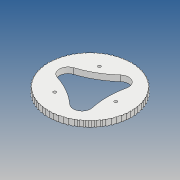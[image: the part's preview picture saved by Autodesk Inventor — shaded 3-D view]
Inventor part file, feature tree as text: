
AUTODESK INVENTOR PART (.ipt)
format: ipt  version: 2017 (Build 210142000, 142)  size: 314,368 bytes
history: native  units: mm
features: other x3, extrude x3, sketch x3
ambient origin geometry x8: Origin, YZ Plane, XZ Plane, XY Plane, X Axis, Y Axis, Z Axis, Center Point
bodies: Body1 (feature_tree)
feature tree (9):
  other  "Sólido1"
  extrude  "Extrusión1"  Depth=6.0mm TaperAngle=0.0deg
  extrude  "Extrusión2"  Depth=5.5mm
  extrude  "Extrusión3"  Depth=1.5mm
  sketch  "Boceto1"  dims[d0=92.093468mm d1=6.0mm d2=0.0mm]
  sketch  "Boceto2"  dims[d4=3.0mm d5=0.0mm d6=5.5mm]
  other  "Sólido2"
  sketch  "Boceto3"  dims[d7=3.0mm d8=0.0mm d9=1.5mm d11=72.0mm d20=61.914795mm d21=172.715906mm d22=68.684649mm d23=24.45mm d24=640.0mm d26=360.0deg d28=4.199872mm d30=83.0mm d31=4.0mm]
  other  "Sólido3"
